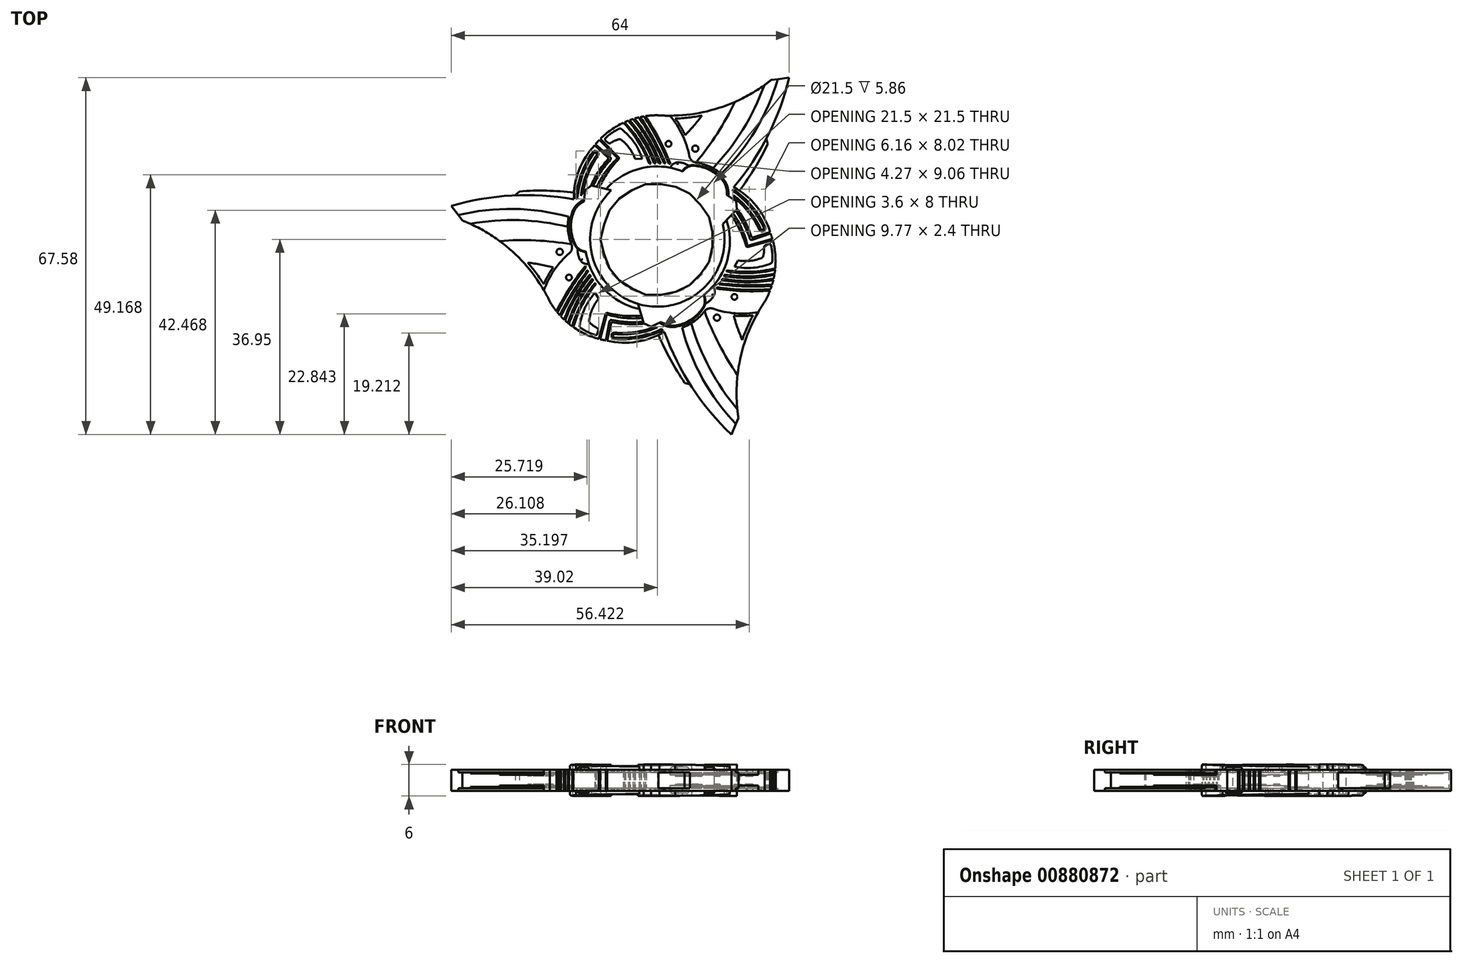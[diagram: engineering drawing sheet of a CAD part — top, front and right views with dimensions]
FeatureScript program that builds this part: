
annotation { "Feature Type Name" : "Feature", "Feature Type Description" : "" }
export const myFeature = defineFeature(function(context is Context, id is Id, definition is map)
    precondition{}
    {
        {
            var Q0;
            Q0=qCreatedBy(makeId("Top.planeOp"),FACE);
            var sketch = newSketch(context, id + "F0", { "sketchPlane" : qUnion([Q0])});
            skCircle(sketch, "E0", {"center": v(0, 0) * mm, "radius": 10.75 * mm});
            skCircle(sketch, "E1", {"center": v(0, 0) * mm, "radius": 12.75 * mm});
            skCircle(sketch, "E2", {"center": v(0, 0) * mm, "radius": 9.75 * mm});
            skSolve(sketch);
        }
        {
            var Q0;
            Q0=makeQuery(id+"F0.imprint","IMPRINT",FACE,{"disambiguationData":[TD([[makeQuery(id+"F0.imprint","IMPRINT",EDGE,{"derivedFrom":sQuery(id+"F0.wireOp",EDGE,"E0")}),-1.0]])]});
            var Q1;
            Q1=makeQuery(id+"F0.imprint","IMPRINT",FACE,{"disambiguationData":[TD([[makeQuery(id+"F0.imprint","IMPRINT",EDGE,{"derivedFrom":sQuery(id+"F0.wireOp",EDGE,"E0")}),1.0]])]});
            extrude(context, id + "F1", {"entities" : qUnion([Q0, Q1]), "endBound" : BoundingType.SYMMETRIC, "oppositeDirection" : true, "depth" : 9 * mm, "offsetDistance" : 25 * mm});
        }
        {
            var Q0;
            Q0=makeQuery(id+"F0.imprint","IMPRINT",FACE,{"disambiguationData":[TD([[makeQuery(id+"F0.imprint","IMPRINT",EDGE,{"derivedFrom":sQuery(id+"F0.wireOp",EDGE,"E0")}),1.0]])]});
            extrude(context, id + "F2", {"entities" : qUnion([Q0]), "operationType" : NewBodyOperationType.REMOVE, "depth" : 7 * mm, "offsetDistance" : 25 * mm});
        }
        {
            var Q0;
            Q0=qCreatedBy(makeId("Top.planeOp"),FACE);
            var sketch = newSketch(context, id + "F3", { "sketchPlane" : qUnion([Q0])});
            skCircle(sketch, "E3", {"center": v(0, 0) * mm, "radius": 10.25 * mm});
            skArc(sketch, "E4", {"start": v(-2, 8) * mm, "mid": v(-8.25, 0) * mm, "end": v(-2, -8) * mm});
            skLineSegment(sketch, "E5.left", {"start": v(-2, 8) * mm, "end": v(-2, -8) * mm});
            skLineSegment(sketch, "E5.right", {"start": v(2, 8) * mm, "end": v(2, -8) * mm});
            skLineSegment(sketch, "E6", {"start": v(-2, 8) * mm, "end": v(2, -8) * mm, "construction": true});
            skArc(sketch, "E7.trimOffspring", {"start": v(2, -8) * mm, "mid": v(8.25, 0) * mm, "end": v(2, 8) * mm});
            skSolve(sketch);
        }
        {
            var Q0;
            Q0=makeQuery(id+"F3.imprint","IMPRINT",FACE,{"disambiguationData":[TD([[makeQuery(id+"F3.imprint","IMPRINT",EDGE,{"derivedFrom":sQuery(id+"F3.wireOp",EDGE,"E3")}),1.0]])]});
            extrude(context, id + "F4", {"entities" : qUnion([Q0]), "oppositeDirection" : true, "depth" : 2 * mm, "offsetDistance" : 25 * mm});
        }
        {
            var Q0;
            Q0=makeQuery(id+"F4.opExtrude","SWEPT_BODY",BODY,{"disambiguationData":[OSD([sQuery(id+"F3.wireOp",EDGE,"E3"),sQuery(id+"F3.wireOp",EDGE,"E4"),sQuery(id+"F3.wireOp",EDGE,"E5.left"),sQuery(id+"F3.wireOp",EDGE,"E5.right"),sQuery(id+"F3.wireOp",EDGE,"E7.trimOffspring")])]});
            deleteBodies(context, id + "F5", {"entities" : qUnion([Q0])});
        }
        {
            var Q0;
            Q0=makeQuery(id+"F0.imprint","IMPRINT",FACE,{"disambiguationData":[TD([[makeQuery(id+"F0.imprint","IMPRINT",EDGE,{"derivedFrom":sQuery(id+"F0.wireOp",EDGE,"E0")}),1.0]])]});
            extrude(context, id + "F6", {"entities" : qUnion([Q0]), "operationType" : NewBodyOperationType.REMOVE, "oppositeDirection" : true, "depth" : 3.5 * mm, "offsetDistance" : 25 * mm});
        }
        {
            var Q0;
            Q0=qCreatedBy(makeId("Top.planeOp"),FACE);
            var sketch = newSketch(context, id + "F7", { "sketchPlane" : qUnion([Q0])});
            skCircle(sketch, "E8.cCircle", {"center": v(0, 0) * mm, "radius": 12.75 * mm});
            skLineSegment(sketch, "E8.0", {"start": v(-12.75, 0) * mm, "end": v(6.38, 11.04) * mm, "construction": true});
            skLineSegment(sketch, "E8.1", {"start": v(6.37, 11.04) * mm, "end": v(6.38, -11.04) * mm, "construction": true});
            skLineSegment(sketch, "E8.2", {"start": v(6.38, -11.04) * mm, "end": v(-12.75, 0) * mm, "construction": true});
            skCircle(sketch, "E9.0", {"center": v(0, 0) * mm, "radius": 12.75 * mm, "construction": true});
            skArc(sketch, "E10", {"start": v(0, 23.52) * mm, "mid": v(-1.13, 23.48) * mm, "end": v(-2.26, 23.35) * mm});
            skArc(sketch, "E11", {"start": v(0, 23.52) * mm, "mid": v(11.42, 24.82) * mm, "end": v(21.58, 30.2) * mm});
            skLineSegment(sketch, "E12", {"start": v(21.58, 30.2) * mm, "end": v(24.98, 30.63) * mm});
            skArc(sketch, "E13", {"start": v(14.56, 10) * mm, "mid": v(20.98, 19.7) * mm, "end": v(24.98, 30.63) * mm});
            skLineSegment(sketch, "E14", {"start": v(20.67, 19.1) * mm, "end": v(20.94, 18.08) * mm});
            skArc(sketch, "E15", {"start": v(14.3, 7.63) * mm, "mid": v(17.93, 12.66) * mm, "end": v(20.94, 18.08) * mm});
            skArc(sketch, "E16", {"start": v(12.1, 12.4) * mm, "mid": v(18.62, 20.7) * mm, "end": v(22.83, 30.36) * mm});
            skArc(sketch, "E17", {"start": v(10.53, 13.5) * mm, "mid": v(16.23, 20.84) * mm, "end": v(20.26, 29.2) * mm});
            skArc(sketch, "E18", {"start": v(7.32, 14.55) * mm, "mid": v(11.36, 20.06) * mm, "end": v(14.68, 26.03) * mm});
            skArc(sketch, "E19", {"start": v(6.08, 15.72) * mm, "mid": v(4.73, 19.82) * mm, "end": v(2.38, 23.43) * mm});
            skArc(sketch, "E20", {"start": v(12.1, 12.4) * mm, "mid": v(9.87, 13.84) * mm, "end": v(7.32, 14.55) * mm});
            skArc(sketch, "E21", {"start": v(6.08, 15.72) * mm, "mid": v(6.51, 14.94) * mm, "end": v(7.32, 14.55) * mm});
            skArc(sketch, "E22", {"start": v(5.26, 19.75) * mm, "mid": v(4.42, 21.36) * mm, "end": v(3.4, 22.88) * mm});
            skArc(sketch, "E23", {"start": v(3.4, 22.88) * mm, "mid": v(5.94, 23.07) * mm, "end": v(8.44, 23.46) * mm});
            skArc(sketch, "E24", {"start": v(5.26, 19.75) * mm, "mid": v(6.92, 21.55) * mm, "end": v(8.44, 23.46) * mm});
            skArc(sketch, "E25", {"start": v(2.48, 14.32) * mm, "mid": v(0.36, 18.97) * mm, "end": v(-2.26, 23.35) * mm});
            skArc(sketch, "E26", {"start": v(2.17, 14.35) * mm, "mid": v(0.05, 18.95) * mm, "end": v(-2.56, 23.3) * mm});
            skLineSegment(sketch, "E27", {"start": v(2.48, 14.32) * mm, "end": v(2.17, 14.35) * mm});
            skArc(sketch, "E28", {"start": v(-2.85, 15.27) * mm, "mid": v(-4.42, 18.41) * mm, "end": v(-6.85, 20.94) * mm});
            skArc(sketch, "E29", {"start": v(-7.36, 20.9) * mm, "mid": v(-8.63, 20.16) * mm, "end": v(-9.78, 19.23) * mm});
            skArc(sketch, "E30", {"start": v(-7.32, 18.95) * mm, "mid": v(-8.06, 18.68) * mm, "end": v(-8.75, 18.32) * mm});
            skArc(sketch, "E31", {"start": v(-4.18, 15.24) * mm, "mid": v(-5.24, 17.21) * mm, "end": v(-6.78, 18.84) * mm});
            skArc(sketch, "E32", {"start": v(-6.78, 18.84) * mm, "mid": v(-7.04, 18.97) * mm, "end": v(-7.32, 18.95) * mm});
            skArc(sketch, "E33", {"start": v(-6.85, 20.94) * mm, "mid": v(-7.1, 20.98) * mm, "end": v(-7.36, 20.9) * mm});
            skLineSegment(sketch, "E34", {"start": v(-9.8, 18.74) * mm, "end": v(-9.36, 18.33) * mm});
            skLineSegment(sketch, "E35", {"start": v(-4.18, 15.24) * mm, "end": v(-2.85, 15.27) * mm});
            skArc(sketch, "E36", {"start": v(-9.78, 19.23) * mm, "mid": v(-9.9, 19) * mm, "end": v(-9.8, 18.74) * mm});
            skArc(sketch, "E37", {"start": v(-9.36, 18.33) * mm, "mid": v(-9.06, 18.21) * mm, "end": v(-8.75, 18.32) * mm});
            skCircle(sketch, "E38", {"center": v(7.2, 17.2) * mm, "radius": 0.6 * mm});
            skCircle(sketch, "E39", {"center": v(2.12, 18.1) * mm, "radius": 0.55 * mm});
            skLineSegment(sketch, "E40", {"start": v(-10.8, 19.02) * mm, "end": v(-7.38, 15.63) * mm});
            skLineSegment(sketch, "E41", {"start": v(-10.8, 19.02) * mm, "end": v(-6.53, 23.33) * mm, "construction": true});
            skLineSegment(sketch, "E42", {"start": v(-10.98, 18.83) * mm, "end": v(-7.67, 15.55) * mm});
            skArc(sketch, "E43", {"start": v(-12.7, -1.1) * mm, "mid": v(-13.79, 0) * mm, "end": v(-15.02, 0.93) * mm});
            skArc(sketch, "E44", {"start": v(-12.67, 3.93) * mm, "mid": v(-14.09, 2.62) * mm, "end": v(-15.02, 0.93) * mm});
            skArc(sketch, "E45", {"start": v(4.7, 12.9) * mm, "mid": v(-6.04, 12.38) * mm, "end": v(-12.67, 3.93) * mm});
            skArc(sketch, "E46", {"start": v(14.56, 10) * mm, "mid": v(14.31, 9) * mm, "end": v(14.6, 8) * mm});
            skArc(sketch, "E47", {"start": v(12.67, 11.21) * mm, "mid": v(9.9, 13.36) * mm, "end": v(6.47, 14.07) * mm});
            skArc(sketch, "E48", {"start": v(13.44, 8.22) * mm, "mid": v(13.34, 9.8) * mm, "end": v(12.67, 11.21) * mm});
            skArc(sketch, "E49", {"start": v(6.47, 14.07) * mm, "mid": v(5.47, 13.66) * mm, "end": v(4.7, 12.9) * mm});
            skLineSegment(sketch, "E50", {"start": v(13.44, 8.22) * mm, "end": v(14.92, 7.21) * mm});
            skLineSegment(sketch, "E51", {"start": v(14.92, 7.21) * mm, "end": v(15.05, 5.7) * mm});
            skLineSegment(sketch, "E52", {"start": v(15.05, 5.7) * mm, "end": v(12.41, 2.9) * mm});
            skArc(sketch, "E53", {"start": v(-7.63, 15.26) * mm, "mid": v(-11.33, 10.22) * mm, "end": v(-12.9, 4.17) * mm});
            skArc(sketch, "E54", {"start": v(-7.34, 15.17) * mm, "mid": v(-10.84, 10.16) * mm, "end": v(-12.58, 4.3) * mm});
            skArc(sketch, "E55", {"start": v(-13.08, 3.93) * mm, "mid": v(-13.5, 3.62) * mm, "end": v(-13.86, 3.26) * mm});
            skArc(sketch, "E56", {"start": v(-8.9, 15.08) * mm, "mid": v(-12.4, 9.6) * mm, "end": v(-13.86, 3.26) * mm});
            skArc(sketch, "E57", {"start": v(-11.88, 17.81) * mm, "mid": v(-15.62, 10.26) * mm, "end": v(-14.58, 1.89) * mm});
            skLineSegment(sketch, "E58", {"start": v(-11.88, 17.81) * mm, "end": v(-9.33, 15.47) * mm});
            skLineSegment(sketch, "E59", {"start": v(-8.93, 15.6) * mm, "end": v(-11.7, 18.04) * mm});
            skArc(sketch, "E60", {"start": v(-9.38, 15.14) * mm, "mid": v(-12.9, 9.32) * mm, "end": v(-14.09, 2.62) * mm});
            skArc(sketch, "E61", {"start": v(-13.08, 3.93) * mm, "mid": v(-12.96, 4.03) * mm, "end": v(-12.9, 4.17) * mm});
            skArc(sketch, "E62", {"start": v(-9.38, 15.14) * mm, "mid": v(-9.3, 15.3) * mm, "end": v(-9.33, 15.47) * mm});
            skArc(sketch, "E63", {"start": v(-8.9, 15.08) * mm, "mid": v(-8.8, 15.34) * mm, "end": v(-8.93, 15.6) * mm});
            skArc(sketch, "E64", {"start": v(-7.63, 15.26) * mm, "mid": v(-7.6, 15.41) * mm, "end": v(-7.67, 15.55) * mm});
            skArc(sketch, "E65", {"start": v(-7.34, 15.17) * mm, "mid": v(-7.28, 15.4) * mm, "end": v(-7.38, 15.63) * mm});
            skArc(sketch, "E66", {"start": v(-11.5, 16) * mm, "mid": v(-13.77, 11.46) * mm, "end": v(-14.58, 6.46) * mm});
            skArc(sketch, "E67", {"start": v(-12.02, 16.34) * mm, "mid": v(-14.35, 11.64) * mm, "end": v(-15.2, 6.47) * mm});
            skArc(sketch, "E68", {"start": v(-15.2, 6.47) * mm, "mid": v(-14.9, 6.15) * mm, "end": v(-14.58, 6.46) * mm});
            skArc(sketch, "E69", {"start": v(-11.5, 16) * mm, "mid": v(-11.6, 16.4) * mm, "end": v(-12.02, 16.34) * mm});
            skArc(sketch, "E70.0", {"start": v(-11.24, 15.83) * mm, "mid": v(-13.48, 11.38) * mm, "end": v(-14.28, 6.46) * mm});
            skArc(sketch, "E70.1", {"start": v(-11.24, 15.83) * mm, "mid": v(-11.43, 16.66) * mm, "end": v(-12.27, 16.51) * mm});
            skArc(sketch, "E70.2", {"start": v(-12.27, 16.51) * mm, "mid": v(-14.63, 11.74) * mm, "end": v(-15.5, 6.48) * mm});
            skArc(sketch, "E70.3", {"start": v(-15.5, 6.48) * mm, "mid": v(-14.9, 5.85) * mm, "end": v(-14.28, 6.46) * mm});
            skArc(sketch, "E71", {"start": v(5.99, 13.93) * mm, "mid": v(4.96, 14.45) * mm, "end": v(3.82, 14.58) * mm});
            skArc(sketch, "E72", {"start": v(3.82, 14.58) * mm, "mid": v(3, 14.28) * mm, "end": v(2.47, 13.57) * mm});
            skLineSegment(sketch, "E73", {"start": v(-11.76, 17.7) * mm, "end": v(-11.56, 17.92) * mm});
            skLineSegment(sketch, "E74", {"start": v(-10.84, 18.69) * mm, "end": v(-10.66, 18.87) * mm});
            skLineSegment(sketch, "E75", {"start": v(-2.4, 23.05) * mm, "end": v(-2.1, 23.1) * mm});
            skArc(sketch, "E76", {"start": v(2.17, 14.35) * mm, "mid": v(0.32, 14.41) * mm, "end": v(-1.53, 14.35) * mm});
            skArc(sketch, "E77", {"start": v(-1.53, 14.35) * mm, "mid": v(-3.6, 18.46) * mm, "end": v(-6.43, 22.1) * mm});
            skArc(sketch, "E78", {"start": v(-1.28, 14.36) * mm, "mid": v(-3.34, 18.53) * mm, "end": v(-6.19, 22.2) * mm});
            skArc(sketch, "E79", {"start": v(1.53, 14.38) * mm, "mid": v(-0.62, 18.9) * mm, "end": v(-3.2, 23.18) * mm});
            skArc(sketch, "E80", {"start": v(1.28, 14.4) * mm, "mid": v(-0.9, 18.87) * mm, "end": v(-3.5, 23.11) * mm});
            skArc(sketch, "E81", {"start": v(0.64, 14.41) * mm, "mid": v(-1.5, 18.85) * mm, "end": v(-4.3, 22.9) * mm});
            skArc(sketch, "E82", {"start": v(0.26, 14.41) * mm, "mid": v(-1.79, 18.83) * mm, "end": v(-4.6, 22.8) * mm});
            skArc(sketch, "E83", {"start": v(-0.3, 14.4) * mm, "mid": v(-2.38, 18.74) * mm, "end": v(-5.28, 22.57) * mm});
            skArc(sketch, "E84", {"start": v(-0.62, 14.4) * mm, "mid": v(-2.7, 18.66) * mm, "end": v(-5.5, 22.5) * mm});
            skArc(sketch, "E85", {"start": v(-3.04, 22.95) * mm, "mid": v(-3.2, 22.92) * mm, "end": v(-3.34, 22.89) * mm});
            skArc(sketch, "E86.trimOffspring", {"start": v(-4.14, 22.7) * mm, "mid": v(-4.28, 22.65) * mm, "end": v(-4.43, 22.61) * mm});
            skArc(sketch, "E87.trimOffspring", {"start": v(-5.1, 22.39) * mm, "mid": v(-5.22, 22.35) * mm, "end": v(-5.34, 22.3) * mm});
            skArc(sketch, "E88.trimOffspring", {"start": v(-6.02, 22.03) * mm, "mid": v(-6.14, 21.97) * mm, "end": v(-6.26, 21.92) * mm});
            skArc(sketch, "E89.trimOffspring", {"start": v(-6.43, 22.1) * mm, "mid": v(-8.75, 20.75) * mm, "end": v(-10.8, 19.02) * mm});
            skArc(sketch, "E90.trimOffspring", {"start": v(-5.5, 22.5) * mm, "mid": v(-5.85, 22.35) * mm, "end": v(-6.19, 22.2) * mm});
            skArc(sketch, "E91.trimOffspring", {"start": v(-4.6, 22.8) * mm, "mid": v(-4.94, 22.7) * mm, "end": v(-5.28, 22.57) * mm});
            skArc(sketch, "E92.trimOffspring", {"start": v(-3.5, 23.11) * mm, "mid": v(-3.9, 23.01) * mm, "end": v(-4.3, 22.9) * mm});
            skArc(sketch, "E93.trimOffspring", {"start": v(-2.56, 23.3) * mm, "mid": v(-2.88, 23.24) * mm, "end": v(-3.2, 23.18) * mm});
            skArc(sketch, "E94.trimOffspring", {"start": v(-10.98, 18.83) * mm, "mid": v(-11.35, 18.44) * mm, "end": v(-11.7, 18.04) * mm});
            skSolve(sketch);
        }
        {
            var Q0;
            {var subQ8=sQuery(id+"F7.wireOp",EDGE,"E43");Q0=makeQuery(id+"F7.imprint","IMPRINT",FACE,{"disambiguationData":[TD([[makeQuery(id+"F7.imprint","IMPRINT",EDGE,{"derivedFrom":subQ8}),-1.0]])]});}
            extrude(context, id + "F8", {"entities" : qUnion([Q0]), "endBound" : BoundingType.SYMMETRIC, "depth" : 6 * mm, "offsetDistance" : 25 * mm});
        }
        {
            var Q0;
            {var subQ9=sQuery(id+"F7.wireOp",EDGE,"E16");Q0=makeQuery(id+"F7.imprint","IMPRINT",FACE,{"disambiguationData":[TD([[makeQuery(id+"F7.imprint","IMPRINT",EDGE,{"derivedFrom":subQ9}),-1.0]])]});}
            var Q1;
            {var subQ1=sQuery(id+"F7.wireOp",EDGE,"E57");Q1=makeQuery(id+"F7.imprint","IMPRINT",FACE,{"disambiguationData":[TD([[makeQuery(id+"F7.imprint","IMPRINT",EDGE,{"derivedFrom":subQ1}),1.0]])]});}
            var Q2;
            Q2=makeQuery(id+"F7.imprint","IMPRINT",FACE,{"disambiguationData":[TD([[makeQuery(id+"F7.imprint","IMPRINT",EDGE,{"derivedFrom":sQuery(id+"F7.wireOp",EDGE,"E66")}),-1.0]])]});
            var Q3;
            {var subQ0=sQuery(id+"F7.wireOp",EDGE,"E42");Q3=makeQuery(id+"F7.imprint","IMPRINT",FACE,{"disambiguationData":[TD([[makeQuery(id+"F7.imprint","IMPRINT",EDGE,{"derivedFrom":subQ0}),-1.0]])]});}
            var Q4;
            {var subQ5=sQuery(id+"F7.wireOp",EDGE,"E93.trimOffspring");Q4=makeQuery(id+"F7.imprint","IMPRINT",FACE,{"disambiguationData":[TD([[makeQuery(id+"F7.imprint","IMPRINT",EDGE,{"derivedFrom":subQ5}),1.0]])]});}
            var Q5;
            {var subQ4=sQuery(id+"F7.wireOp",EDGE,"E92.trimOffspring");Q5=makeQuery(id+"F7.imprint","IMPRINT",FACE,{"disambiguationData":[TD([[makeQuery(id+"F7.imprint","IMPRINT",EDGE,{"derivedFrom":subQ4}),1.0]])]});}
            var Q6;
            {var subQ7=sQuery(id+"F7.wireOp",EDGE,"E91.trimOffspring");Q6=makeQuery(id+"F7.imprint","IMPRINT",FACE,{"disambiguationData":[TD([[makeQuery(id+"F7.imprint","IMPRINT",EDGE,{"derivedFrom":subQ7}),1.0]])]});}
            var Q7;
            {var subQ4=sQuery(id+"F7.wireOp",EDGE,"E90.trimOffspring");Q7=makeQuery(id+"F7.imprint","IMPRINT",FACE,{"disambiguationData":[TD([[makeQuery(id+"F7.imprint","IMPRINT",EDGE,{"derivedFrom":subQ4}),1.0]])]});}
            extrude(context, id + "F9", {"entities" : qUnion([Q0, Q1, Q2, Q3, Q4, Q5, Q6, Q7]), "operationType" : NewBodyOperationType.ADD, "endBound" : BoundingType.SYMMETRIC, "depth" : 4 * mm, "offsetDistance" : 25 * mm});
        }
        {
            var Q0;
            {var subQ4=sQuery(id+"F7.wireOp",EDGE,"E71");Q0=makeQuery(id+"F7.imprint","IMPRINT",FACE,{"disambiguationData":[TD([[makeQuery(id+"F7.imprint","IMPRINT",EDGE,{"derivedFrom":subQ4}),1.0]])]});}
            extrude(context, id + "F10", {"entities" : qUnion([Q0]), "operationType" : NewBodyOperationType.ADD, "endBound" : BoundingType.SYMMETRIC, "depth" : 5 * mm, "offsetDistance" : 25 * mm});
        }
        {
            var Q0;
            Q0=makeQuery(id+"F7.imprint","IMPRINT",FACE,{"disambiguationData":[TD([[makeQuery(id+"F7.imprint","IMPRINT",EDGE,{"derivedFrom":sQuery(id+"F7.wireOp",EDGE,"E28")}),1.0]])]});
            var Q1;
            {var subQ5=sQuery(id+"F7.wireOp",EDGE,"E40");Q1=makeQuery(id+"F7.imprint","IMPRINT",FACE,{"disambiguationData":[TD([[makeQuery(id+"F7.imprint","IMPRINT",EDGE,{"derivedFrom":subQ5}),-1.0]])]});}
            var Q2;
            Q2=makeQuery(id+"F7.imprint","IMPRINT",FACE,{"disambiguationData":[TD([[makeQuery(id+"F7.imprint","IMPRINT",EDGE,{"derivedFrom":sQuery(id+"F7.wireOp",EDGE,"E66")}),1.0]])]});
            var Q3;
            Q3=makeQuery(id+"F7.imprint","IMPRINT",FACE,{"disambiguationData":[TD([[makeQuery(id+"F7.imprint","IMPRINT",EDGE,{"derivedFrom":sQuery(id+"F7.wireOp",EDGE,"E39")}),1.0]])]});
            var Q4;
            {var subQ2=sQuery(id+"F7.wireOp",EDGE,"E14");Q4=makeQuery(id+"F7.imprint","IMPRINT",FACE,{"disambiguationData":[TD([[makeQuery(id+"F7.imprint","IMPRINT",EDGE,{"derivedFrom":subQ2}),-1.0]])]});}
            var Q5;
            {var subQ5=sQuery(id+"F7.wireOp",EDGE,"E88.trimOffspring");Q5=makeQuery(id+"F7.imprint","IMPRINT",FACE,{"disambiguationData":[TD([[makeQuery(id+"F7.imprint","IMPRINT",EDGE,{"derivedFrom":subQ5}),1.0]])]});}
            var Q6;
            {var subQ5=sQuery(id+"F7.wireOp",EDGE,"E87.trimOffspring");Q6=makeQuery(id+"F7.imprint","IMPRINT",FACE,{"disambiguationData":[TD([[makeQuery(id+"F7.imprint","IMPRINT",EDGE,{"derivedFrom":subQ5}),1.0]])]});}
            var Q7;
            {var subQ5=sQuery(id+"F7.wireOp",EDGE,"E86.trimOffspring");Q7=makeQuery(id+"F7.imprint","IMPRINT",FACE,{"disambiguationData":[TD([[makeQuery(id+"F7.imprint","IMPRINT",EDGE,{"derivedFrom":subQ5}),1.0]])]});}
            var Q8;
            {var subQ5=sQuery(id+"F7.wireOp",EDGE,"E85");Q8=makeQuery(id+"F7.imprint","IMPRINT",FACE,{"disambiguationData":[TD([[makeQuery(id+"F7.imprint","IMPRINT",EDGE,{"derivedFrom":subQ5}),1.0]])]});}
            var Q9;
            {var subQ0=sQuery(id+"F7.wireOp",EDGE,"E27");Q9=makeQuery(id+"F7.imprint","IMPRINT",FACE,{"disambiguationData":[TD([[makeQuery(id+"F7.imprint","IMPRINT",EDGE,{"derivedFrom":subQ0}),-1.0]])]});}
            var Q10;
            {var subQ1=sQuery(id+"F7.wireOp",EDGE,"E16");Q10=makeQuery(id+"F7.imprint","IMPRINT",FACE,{"disambiguationData":[TD([[makeQuery(id+"F7.imprint","IMPRINT",EDGE,{"derivedFrom":subQ1}),1.0]])]});}
            extrude(context, id + "F11", {"entities" : qUnion([Q0, Q1, Q2, Q3, Q4, Q5, Q6, Q7, Q8, Q9, Q10]), "operationType" : NewBodyOperationType.ADD, "endBound" : BoundingType.SYMMETRIC, "depth" : 3 * mm, "offsetDistance" : 25 * mm});
        }
        {
            var Q0;
            {var subQ0=sQuery(id+"F7.wireOp",EDGE,"E17");Q0=makeQuery(id+"F7.imprint","IMPRINT",FACE,{"disambiguationData":[TD([[makeQuery(id+"F7.imprint","IMPRINT",EDGE,{"derivedFrom":subQ0}),1.0]])]});}
            extrude(context, id + "F12", {"entities" : qUnion([Q0]), "operationType" : NewBodyOperationType.ADD, "endBound" : BoundingType.SYMMETRIC, "depth" : 2.5 * mm, "offsetDistance" : 25 * mm});
        }
        {
            var Q0;
            {var subQ1=sQuery(id+"F7.wireOp",EDGE,"E18");Q0=makeQuery(id+"F7.imprint","IMPRINT",FACE,{"disambiguationData":[TD([[makeQuery(id+"F7.imprint","IMPRINT",EDGE,{"derivedFrom":subQ1}),1.0]])]});}
            extrude(context, id + "F13", {"entities" : qUnion([Q0]), "operationType" : NewBodyOperationType.ADD, "endBound" : BoundingType.SYMMETRIC, "depth" : 2 * mm, "offsetDistance" : 25 * mm});
        }
        {
            var Q0;
            Q0=makeQuery(id+"F7.imprint","IMPRINT",FACE,{"disambiguationData":[TD([[makeQuery(id+"F7.imprint","IMPRINT",EDGE,{"derivedFrom":sQuery(id+"F7.wireOp",EDGE,"E38")}),1.0]])]});
            var Q1;
            Q1=makeQuery(id+"F7.imprint","IMPRINT",FACE,{"disambiguationData":[TD([[makeQuery(id+"F7.imprint","IMPRINT",EDGE,{"derivedFrom":sQuery(id+"F7.wireOp",EDGE,"E22")}),-1.0]])]});
            extrude(context, id + "F14", {"entities" : qUnion([Q0, Q1]), "operationType" : NewBodyOperationType.ADD, "endBound" : BoundingType.SYMMETRIC, "depth" : 1.5 * mm, "offsetDistance" : 25 * mm});
        }
        {
            var Q0;
            Q0=makeQuery(id+"F8.opExtrude","CAP_EDGE",EDGE,{"disambiguationData":[OSD([sQuery(id+"F7.wireOp",EDGE,"E49")])],"isStart":false});
            var Q1;
            Q1=makeQuery(id+"F8.opExtrude","CAP_EDGE",EDGE,{"disambiguationData":[OSD([sQuery(id+"F7.wireOp",EDGE,"E47")])],"isStart":false});
            var Q2;
            Q2=makeQuery(id+"F8.opExtrude","CAP_EDGE",EDGE,{"disambiguationData":[OSD([sQuery(id+"F7.wireOp",EDGE,"E48")])],"isStart":false});
            var Q3;
            Q3=makeQuery(id+"F10.opExtrude","CAP_EDGE",EDGE,{"disambiguationData":[OSD([sQuery(id+"F7.wireOp",EDGE,"E71")])],"isStart":false});
            var Q4;
            Q4=makeQuery(id+"F10.opExtrude","CAP_EDGE",EDGE,{"disambiguationData":[OSD([sQuery(id+"F7.wireOp",EDGE,"E72")])],"isStart":false});
            var Q5;
            Q5=makeQuery(id+"F10.opExtrude","CAP_EDGE",EDGE,{"disambiguationData":[OSD([sQuery(id+"F7.wireOp",EDGE,"E72")])],"isStart":true});
            var Q6;
            Q6=makeQuery(id+"F10.opExtrude","CAP_EDGE",EDGE,{"disambiguationData":[OSD([sQuery(id+"F7.wireOp",EDGE,"E71")])],"isStart":true});
            var Q7;
            Q7=makeQuery(id+"F8.opExtrude","CAP_EDGE",EDGE,{"disambiguationData":[OSD([sQuery(id+"F7.wireOp",EDGE,"E49")])],"isStart":true});
            var Q8;
            Q8=makeQuery(id+"F8.opExtrude","CAP_EDGE",EDGE,{"disambiguationData":[OSD([sQuery(id+"F7.wireOp",EDGE,"E47")])],"isStart":true});
            var Q9;
            Q9=makeQuery(id+"F8.opExtrude","CAP_EDGE",EDGE,{"disambiguationData":[OSD([sQuery(id+"F7.wireOp",EDGE,"E48")])],"isStart":true});
            fillet(context, id + "F15", {"entities" : qUnion([Q0, Q1, Q2, Q3, Q4, Q5, Q6, Q7, Q8, Q9]), "radius" : .45 * mm, "tangentPropagation" : true, "allowEdgeOverflow" : false});
        }
        {
            var Q0;
            Q0=qCreatedBy(makeId("Front.planeOp"),FACE);
            var sketch = newSketch(context, id + "F16", { "sketchPlane" : qUnion([Q0])});
            skLineSegment(sketch, "E95.0", {"start": v(-12.75, 4.5) * mm, "end": v(12.75, 4.5) * mm, "construction": true});
            skLineSegment(sketch, "E96", {"start": v(-15.02, 2.5) * mm, "end": v(15.05, 3) * mm});
            skLineSegment(sketch, "E97.0", {"start": v(15.05, 3) * mm, "end": v(15.05, -3) * mm, "construction": true});
            skLineSegment(sketch, "E98", {"start": v(15.05, 3) * mm, "end": v(18.67, 3) * mm});
            skLineSegment(sketch, "E99", {"start": v(18.67, 3) * mm, "end": v(15.55, 6.61) * mm});
            skLineSegment(sketch, "E100", {"start": v(15.55, 6.61) * mm, "end": v(-16.77, 6.35) * mm});
            skLineSegment(sketch, "E101", {"start": v(-16.77, 6.35) * mm, "end": v(-15.02, 2.5) * mm});
            skLineSegment(sketch, "E102.0.0", {"start": v(5.53, 2.5) * mm, "end": v(3.85, 2.5) * mm, "construction": true});
            skLineSegment(sketch, "E102.0.1", {"start": v(3.85, 2.5) * mm, "end": v(2.92, 2.5) * mm, "construction": true});
            skLineSegment(sketch, "E102.0.2", {"start": v(2.92, 2.5) * mm, "end": v(4.7, 2.5) * mm, "construction": true});
            skLineSegment(sketch, "E102.0.3", {"start": v(4.7, 2.5) * mm, "end": v(5.53, 2.5) * mm, "construction": true});
            skPoint(sketch, "E103.0", {"position": v(21.58, 0) * mm});
            skPoint(sketch, "E104.0", {"position": v(0, 0) * mm});
            skLineSegment(sketch, "E105", {"start": v(21.58, 0) * mm, "end": v(0, 0) * mm, "construction": true});
            skLineSegment(sketch, "E106.MirrorCS", {"start": v(18.67, -3) * mm, "end": v(15.55, -6.61) * mm});
            skLineSegment(sketch, "E107.MirrorCS", {"start": v(15.05, -3) * mm, "end": v(18.67, -3) * mm});
            skLineSegment(sketch, "E108.MirrorCS", {"start": v(-15.02, -2.5) * mm, "end": v(15.05, -3) * mm});
            skLineSegment(sketch, "E109.MirrorCS", {"start": v(15.55, -6.61) * mm, "end": v(-16.77, -6.35) * mm});
            skLineSegment(sketch, "E110.MirrorCS", {"start": v(-16.77, -6.35) * mm, "end": v(-15.02, -2.5) * mm});
            skSolve(sketch);
        }
        {
            var Q0;
            Q0=makeQuery(id+"F16.imprint","IMPRINT",FACE,{"disambiguationData":[TD([[makeQuery(id+"F16.imprint","IMPRINT",EDGE,{"derivedFrom":sQuery(id+"F16.wireOp",EDGE,"E96")}),1.0]])]});
            var Q1;
            Q1=makeQuery(id+"F16.imprint","IMPRINT",FACE,{"disambiguationData":[TD([[makeQuery(id+"F16.imprint","IMPRINT",EDGE,{"derivedFrom":sQuery(id+"F16.wireOp",EDGE,"E106.MirrorCS")}),-1.0]])]});
            extrude(context, id + "F17", {"entities" : qUnion([Q0, Q1]), "operationType" : NewBodyOperationType.REMOVE, "endBound" : BoundingType.SYMMETRIC, "oppositeDirection" : true, "depth" : 50 * mm, "offsetDistance" : 25 * mm});
        }
        {
            var Q0;
            Q0=makeQuery(id+"F8.opExtrude","SWEPT_BODY",BODY,{"disambiguationData":[OSD([sQuery(id+"F7.wireOp",EDGE,"E8.cCircle"),sQuery(id+"F7.wireOp",EDGE,"E43"),sQuery(id+"F7.wireOp",EDGE,"E44"),sQuery(id+"F7.wireOp",EDGE,"E45"),sQuery(id+"F7.wireOp",EDGE,"E47"),sQuery(id+"F7.wireOp",EDGE,"E48"),sQuery(id+"F7.wireOp",EDGE,"E49"),sQuery(id+"F7.wireOp",EDGE,"E50"),sQuery(id+"F7.wireOp",EDGE,"E51"),sQuery(id+"F7.wireOp",EDGE,"E52")])]});
            var Q1;
            Q1=makeQuery(id+"F1.opExtrude","SWEPT_FACE",FACE,{"disambiguationData":[OSD([sQuery(id+"F0.wireOp",EDGE,"E1")])]});
            circularPattern(context, id + "F18", {"operationType" : NewBodyOperationType.ADD, "entities" : qUnion([Q0]), "axis" : qUnion([Q1]), "angle" : 360 * degree, "instanceCount" : 3, "equalSpace" : true});
        }
    });
